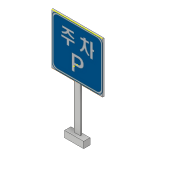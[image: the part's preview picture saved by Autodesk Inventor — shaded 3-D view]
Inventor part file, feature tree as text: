
AUTODESK INVENTOR PART (.ipt)
format: ipt  version: 2018 (Build 220112000, 112)  size: 166,912 bytes
history: native  units: in
note: dims shown in document units (in); Inventor stores cm internally (conversion verified against a paired STEP export)
features: sketch x5, extrude x3, other x1
ambient origin geometry x8: Origin, YZ Plane, XZ Plane, XY Plane, X Axis, Y Axis, Z Axis, Center Point
bodies: Solid1 (feature_tree)
feature tree (9):
  extrude  "Extrusion1"  Depth=0.0787in TaperAngle=0.0deg
  sketch  "Sketch2"  dims[d12=0.3937in d13=2.7559in]
  extrude  "Extrusion2"  Depth=2.7559in
  sketch  "Sketch4"  dims[d16=0.3937in]
  extrude  "Extrusion3"  Depth=1.1811in
  sketch  "Sketch1"  dims[d8=0.9583in d9=0.0787in d10=0.0in]
  sketch  "Sketch3"  dims[d14=0.1969in d15=1.1811in]
  sketch  "Sketch7"  dims[d17=0.3937in d18=0.0in d21=0.3937in d22=0.0787in d23=0.0in]
  other  "Image6"
